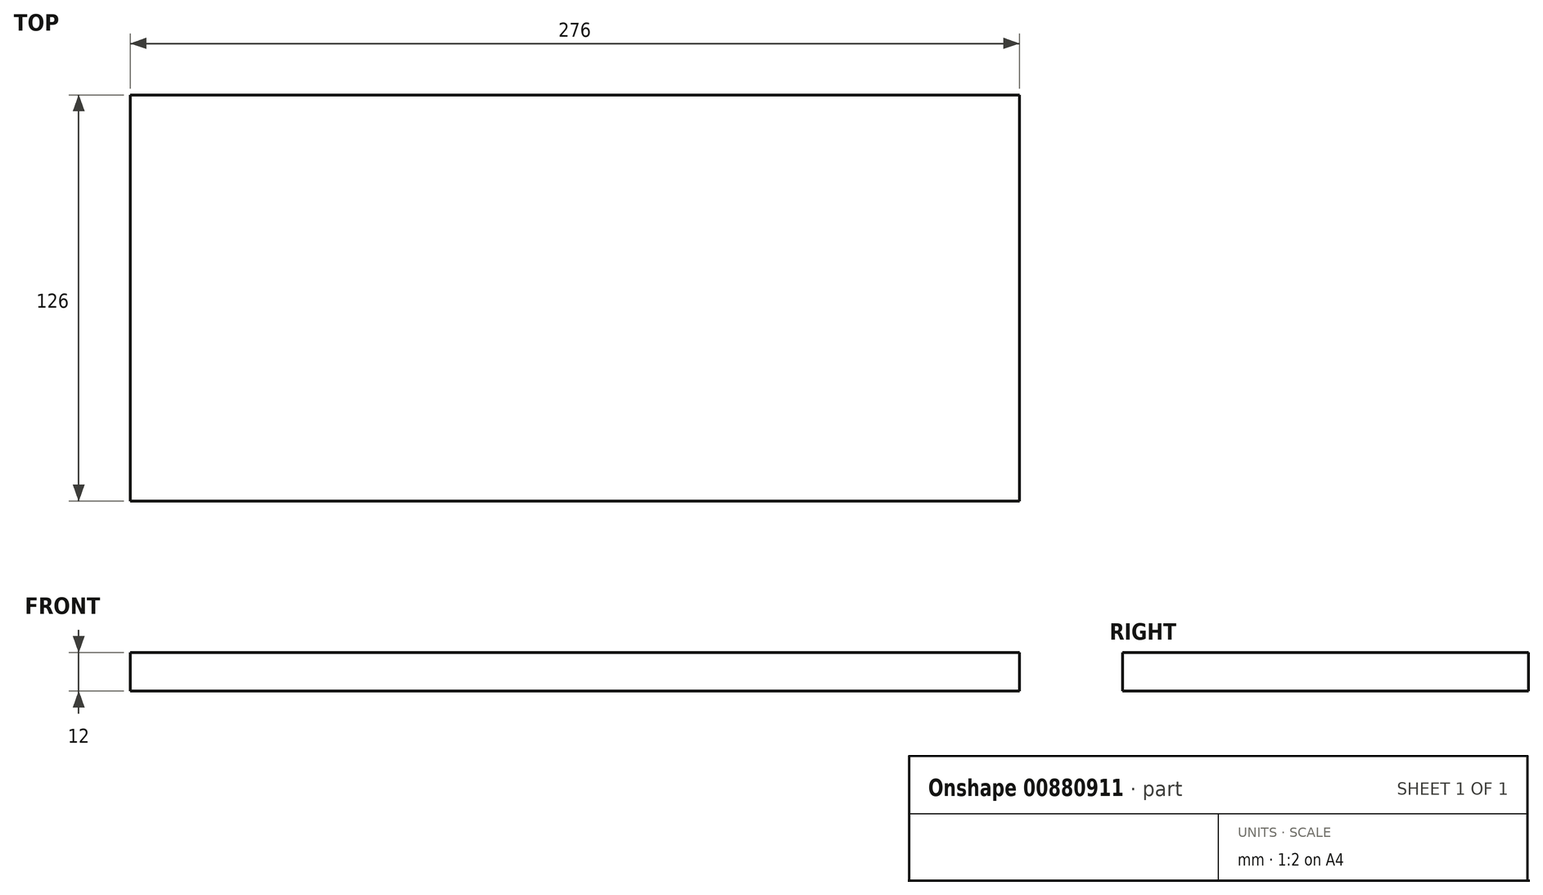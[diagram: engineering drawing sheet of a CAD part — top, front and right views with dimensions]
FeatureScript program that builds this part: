
annotation { "Feature Type Name" : "Feature", "Feature Type Description" : "" }
export const myFeature = defineFeature(function(context is Context, id is Id, definition is map)
    precondition{}
    {
        {
            var Q0;
            Q0=qCreatedBy(makeId("Top.planeOp"),FACE);
            var sketch = newSketch(context, id + "F0", { "sketchPlane" : qUnion([Q0])});
            skLineSegment(sketch, "E0.bottom", {"start": v(141.44, -63) * mm, "end": v(-134.56, -63) * mm});
            skLineSegment(sketch, "E0.top", {"start": v(141.44, 63) * mm, "end": v(-134.56, 63) * mm});
            skLineSegment(sketch, "E0.left", {"start": v(141.44, -63) * mm, "end": v(141.44, 63) * mm});
            skLineSegment(sketch, "E0.right", {"start": v(-134.56, -63) * mm, "end": v(-134.56, 63) * mm});
            skPoint(sketch, "E0.middle", {"position": v(3.44, 0) * mm});
            skSolve(sketch);
        }
        {
            var Q0;
            Q0=makeQuery(id+"F0.imprint","IMPRINT",FACE,{"disambiguationData":[TD([[makeQuery(id+"F0.imprint","IMPRINT",EDGE,{"derivedFrom":sQuery(id+"F0.wireOp",EDGE,"E0.bottom")}),-1.0]])]});
            extrude(context, id + "F1", {"entities" : qUnion([Q0]), "depth" : 12 * mm, "offsetDistance" : 25 * mm});
        }
    });
